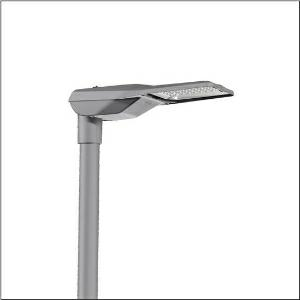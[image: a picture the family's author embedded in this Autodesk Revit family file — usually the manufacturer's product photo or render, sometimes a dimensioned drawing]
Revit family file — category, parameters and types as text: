
# Revit family: streetlight_sl_21_mini___pl52_5xe2h33s08hb_6ab9
name_source: partatom
category: Lighting Fixtures
units: mm (PartAtom-declared; Revit-internal decimal feet)

## family parameters
Cut with Voids When Loaded = No
Host = Face
Light Source = No
Part Type = Normal
Room Calculation Point = No
Round Connector Dimension = Use Diameter
Shared = No

## types (1)
- --- (1 x LED, 8890 lm, 66 W, 3000K)
    Apparent Load = 66 VA
    CIE Flux Codes = 27 59 98 100 100
    Color Rendering = 70
    Color Temperature = 3000K
    Default Elevation = 1800 mm
    Description = Streetlight SL 21 mini, mast luminaire, primary light control with lens, of PMMA, primary optical cover: cover, of toughened safety glass, transparent, light distribution: PL52, light emission: direct distribution, primary light characteristic: asymmetric, installation type: side-entry, post-top, LED, High Power LED, rated luminous flux: 8.890lm, luminous efficacy: 135lm/W, light colour: 730, colour temperature: 3000K, control gear: D4i, control: overheat protection, constant luminous flux control, time-dependent luminous flux control, flexible luminous flux parameterisation, pre-setting: logarithmic dimming characteristic, mains connection: 220..240V, AC, 50/60Hz, start of lifetime: 66W, end of service life: 69W, reduction: 30W, luminaire housing, of diecast aluminium, powder-coated, Siteco® metallic grey (DB 702S), corrosivity category C5 mid according to DIN EN ISO 12944, please order mast flange separately, inclination adjustable: 0°, 5°, 10°, 15°, sealing non-destructively replaceable, multi-level sealing system, length: 628mm, width: 235mm, height: 110mm, mast flange for spigot size: 42mm (side-entry): 5XC10008XM4, 60/48mm (side-entry/post-top): 5XC10108XM2, 76/60mm (side-entry/post-top): 5XC10108XM1, mounting height: 4..8m, Smart Interface above, protection rating (complete): IP66, insulation class (complete): insulation class II (safety insulation), certification: CE, ENEC, ENEC+, VDE, impact resistance: IK10, permissible operating ambient temperature for outdoor applications: -40..+50°C, standard-compliant lighting for roads and squares, packaging unit: 1 piece

Light Distribution: PL52
    Height = 110 mm
    Lamp = 1 x LED
    Lamp Light Flux = 8890 lm
    Lamp Power = 66 W
    Lamp count = 1
    Length = 625 mm
    Luminous efficacy = 135 lm/W
    Manufacturer = Siteco
    ModVariant = No
    Model = 5XE2H33S08HB
    Number of Poles = 1
    OnlyDefault = Yes
    Power Factor = 1
    Product Name = Streetlight SL 21 mini | PL52
    Product group = mast luminaire | pylon top
    ProductGroupID = 6100
    Protection Class = Protection class II
    Protection Degree = IP 66
    RLX_Detail_Level = 1
    RLX_Emergency_Light_Flux = 0 lm
    RLX_Emergency_Type = 0
    RLX_Emergency_Type_DB = No
    RlxData = <blob elided: 35689 chars, md5=43be4b5a>
    Socket = socket
    Standby Power = 0 W
    System Light Flux = 8890 lm
    System Power = 66 W
    Type Comments = factory setting: luminous flux: 100 % | dim-lin: 254 | 670 mA
    Type Image = l_1003515.jpg
    URL = http://relux.com
    VarID = @adj_211431
    Voltage = 0 V
    Weight = 0.00 kg
    Width = 234 mm

## geometry (parser evidence)
native form markers: Blend x4, Sweep x11
no freeform markers — native parametric forms only
